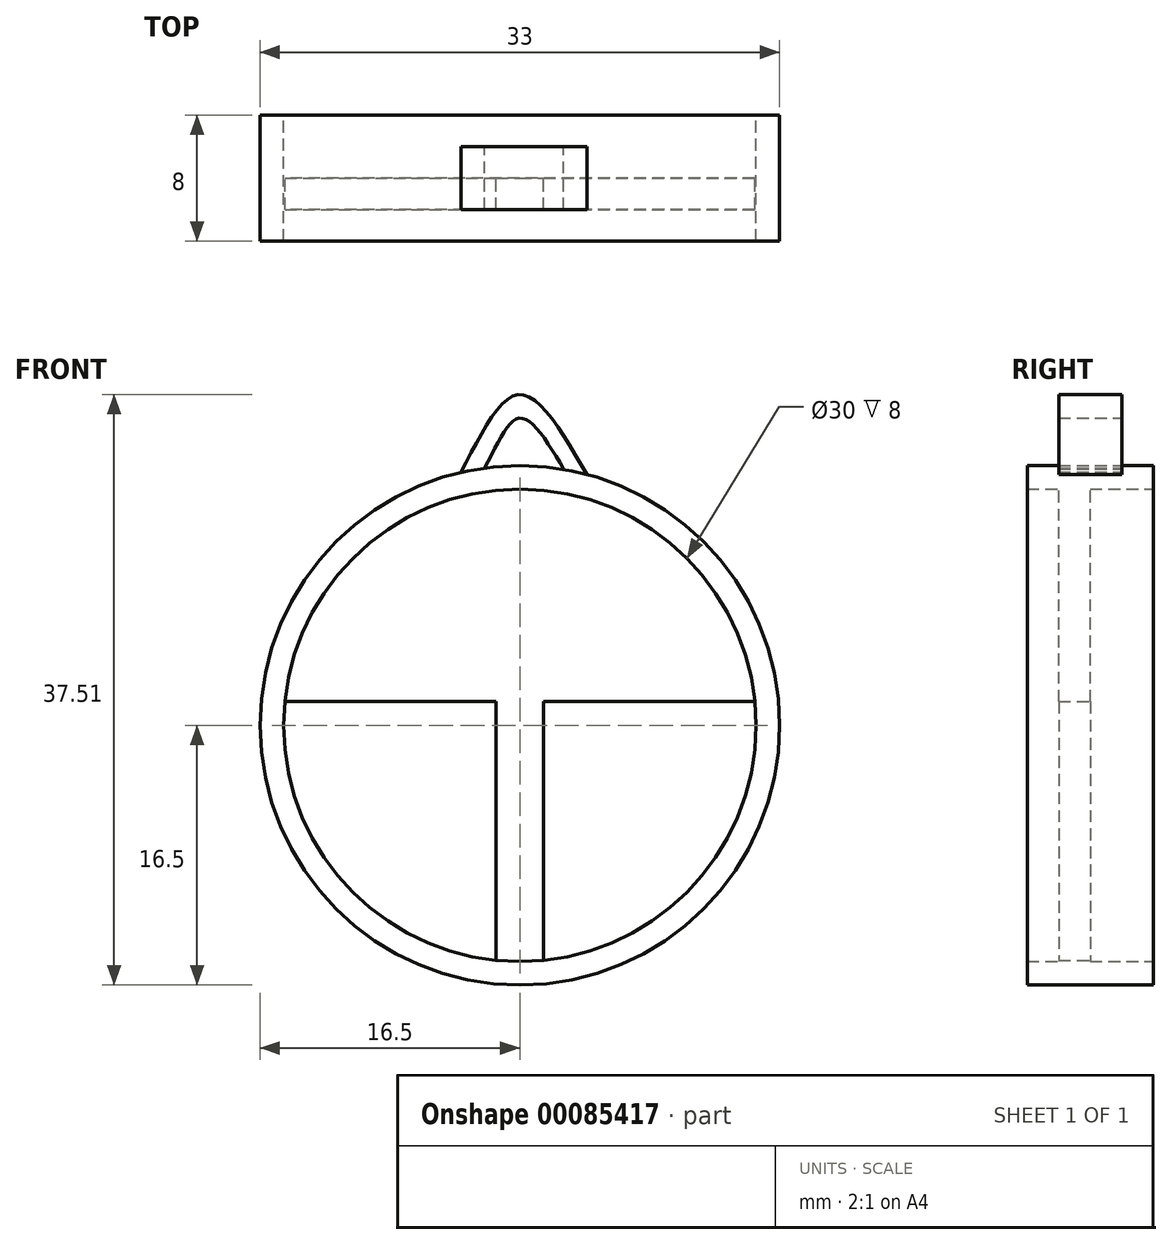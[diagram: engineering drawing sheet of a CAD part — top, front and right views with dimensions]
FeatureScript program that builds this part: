
annotation { "Feature Type Name" : "Feature", "Feature Type Description" : "" }
export const myFeature = defineFeature(function(context is Context, id is Id, definition is map)
    precondition{}
    {
        {
            var Q0;
            Q0=qCreatedBy(makeId("Front.planeOp"),FACE);
            var sketch = newSketch(context, id + "F0", { "sketchPlane" : qUnion([Q0])});
            skCircle(sketch, "E0", {"center": v(0, 0) * mm, "radius": 15 * mm});
            skCircle(sketch, "E1", {"center": v(0, 0) * mm, "radius": 16.5 * mm});
            skLineSegment(sketch, "E2", {"start": v(-14.92, 1.5) * mm, "end": v(14.92, 1.5) * mm});
            skLineSegment(sketch, "E3", {"start": v(-14.92, -1.5) * mm, "end": v(14.92, -1.5) * mm});
            skLineSegment(sketch, "E4", {"start": v(-1.5, 14.92) * mm, "end": v(-1.5, -14.92) * mm});
            skLineSegment(sketch, "E5", {"start": v(1.5, 14.92) * mm, "end": v(1.5, -14.92) * mm});
            skFitSpline(sketch, "E6", {"points": [v(-2.26, 16.34) * mm, v(0, 19.51) * mm, v(2.78, 16.26) * mm], "startDerivative": vector(5.46, 9.74) * mm, "endDerivative": vector(5.58, -9.73) * mm});
            skFitSpline(sketch, "E7", {"points": [v(-3.73, 16.07) * mm, v(0, 21.01) * mm, v(4.25, 15.94) * mm], "startDerivative": vector(7.4, 14.24) * mm, "endDerivative": vector(8.41, -14.3) * mm});
            skSolve(sketch);
        }
        {
            var Q0;
            {var subQ0=sQuery(id+"F0.wireOp",EDGE,"E2");var subQ1=sQuery(id+"F0.wireOp",EDGE,"E0");var subQ2=makeQuery(id+"F0.imprint","INTERSECT",VERTEX,{"disambiguationData":[OD(1.0)],"derivedFrom":[subQ1,subQ0]});Q0=makeQuery(id+"F0.imprint","IMPRINT",FACE,{"disambiguationData":[TD([[makeQuery(id+"F0.imprint","IMPRINT",EDGE,{"disambiguationData":[TD([[subQ2,-1.0]])],"derivedFrom":subQ1}),-1.0]])]});}
            extrude(context, id + "F1", {"entities" : qUnion([Q0]), "endBound" : BoundingType.SYMMETRIC, "depth" : 8 * mm});
        }
        {
            var Q0;
            Q0 = qSketchRegion(id + "F0", true);
            extrude(context, id + "F2", {"entities" : qUnion([Q0]), "operationType" : NewBodyOperationType.ADD, "endBound" : BoundingType.SYMMETRIC, "depth" : 4 * mm});
        }
        {
            var Q0;
            {var subQ0=sQuery(id+"F0.wireOp",EDGE,"E4");var subQ1=sQuery(id+"F0.wireOp",EDGE,"E0");var subQ2=makeQuery(id+"F0.imprint","INTERSECT",VERTEX,{"disambiguationData":[OD(0.0)],"derivedFrom":[subQ1,subQ0]});Q0=makeQuery(id+"F0.imprint","IMPRINT",FACE,{"disambiguationData":[TD([[makeQuery(id+"F0.imprint","IMPRINT",EDGE,{"disambiguationData":[TD([[subQ2,1.0]])],"derivedFrom":subQ1}),1.0]])]});}
            var Q1;
            {var subQ0=sQuery(id+"F0.wireOp",EDGE,"E2");var subQ1=sQuery(id+"F0.wireOp",EDGE,"E0");var subQ2=makeQuery(id+"F0.imprint","INTERSECT",VERTEX,{"disambiguationData":[OD(0.0)],"derivedFrom":[subQ1,subQ0]});Q1=makeQuery(id+"F0.imprint","IMPRINT",FACE,{"disambiguationData":[TD([[makeQuery(id+"F0.imprint","IMPRINT",EDGE,{"disambiguationData":[TD([[subQ2,-1.0]])],"derivedFrom":subQ1}),1.0]])]});}
            var Q2;
            {var subQ0=sQuery(id+"F0.wireOp",EDGE,"E2");var subQ1=sQuery(id+"F0.wireOp",EDGE,"E0");var subQ2=makeQuery(id+"F0.imprint","INTERSECT",VERTEX,{"disambiguationData":[OD(1.0)],"derivedFrom":[subQ1,subQ0]});Q2=makeQuery(id+"F0.imprint","IMPRINT",FACE,{"disambiguationData":[TD([[makeQuery(id+"F0.imprint","IMPRINT",EDGE,{"disambiguationData":[TD([[subQ2,1.0]])],"derivedFrom":subQ1}),1.0]])]});}
            var Q3;
            {var subQ0=sQuery(id+"F0.wireOp",EDGE,"E4");var subQ1=sQuery(id+"F0.wireOp",EDGE,"E0");var subQ2=makeQuery(id+"F0.imprint","INTERSECT",VERTEX,{"disambiguationData":[OD(1.0)],"derivedFrom":[subQ1,subQ0]});Q3=makeQuery(id+"F0.imprint","IMPRINT",FACE,{"disambiguationData":[TD([[makeQuery(id+"F0.imprint","IMPRINT",EDGE,{"disambiguationData":[TD([[subQ2,-1.0]])],"derivedFrom":subQ1}),1.0]])]});}
            var Q4;
            {var subQ0=sQuery(id+"F0.wireOp",EDGE,"E4");var subQ1=sQuery(id+"F0.wireOp",EDGE,"E2");var subQ2=makeQuery(id+"F0.imprint","INTERSECT",VERTEX,{"derivedFrom":[subQ1,subQ0]});Q4=makeQuery(id+"F0.imprint","IMPRINT",FACE,{"disambiguationData":[TD([[makeQuery(id+"F0.imprint","IMPRINT",EDGE,{"disambiguationData":[TD([[subQ2,-1.0]])],"derivedFrom":subQ1}),-1.0]])]});}
            extrude(context, id + "F3", {"entities" : qUnion([Q0, Q1, Q2, Q3, Q4]), "operationType" : NewBodyOperationType.ADD, "depth" : 2 * mm});
        }
    });
